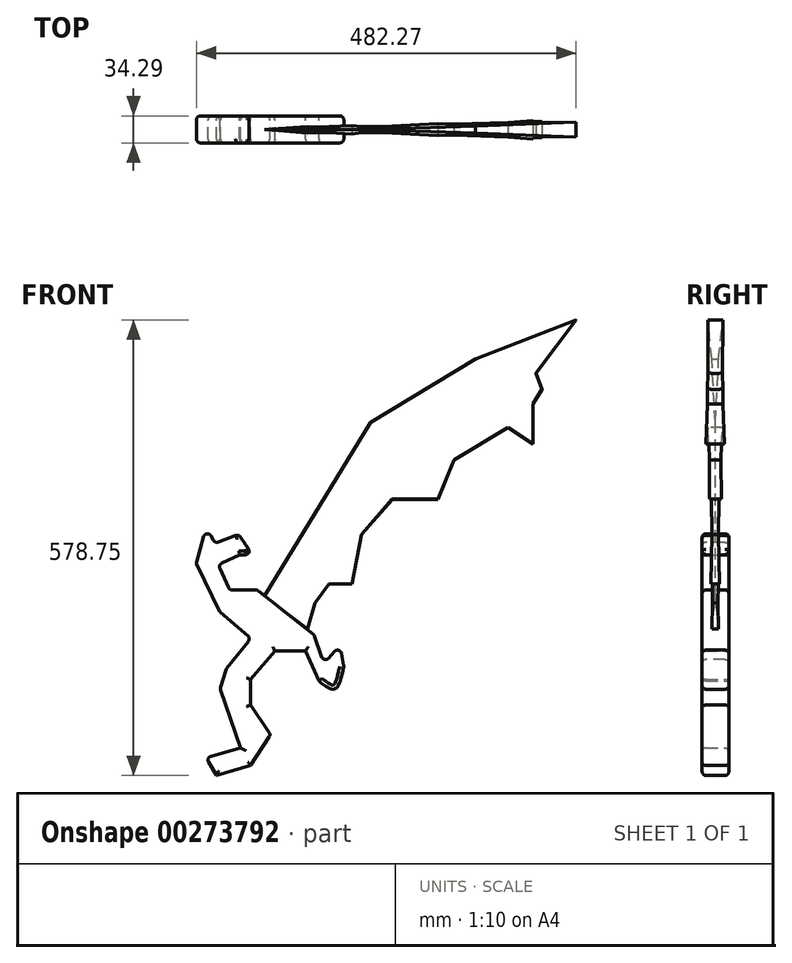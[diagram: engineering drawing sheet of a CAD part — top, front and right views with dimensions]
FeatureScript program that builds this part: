
annotation { "Feature Type Name" : "Feature", "Feature Type Description" : "" }
export const myFeature = defineFeature(function(context is Context, id is Id, definition is map)
    precondition{}
    {
        {
            var Q0;
            Q0=qCreatedBy(makeId("Front.planeOp"),FACE);
            var sketch = newSketch(context, id + "F0", { "sketchPlane" : qUnion([Q0])});
            skLineSegment(sketch, "E0", {"start": v(-57, -87.42) * mm, "end": v(-43.3, -110.26) * mm});
            skLineSegment(sketch, "E1", {"start": v(-43.3, -110.26) * mm, "end": v(0, -97.55) * mm});
            skLineSegment(sketch, "E2", {"start": v(0, -97.55) * mm, "end": v(25.23, -58.18) * mm});
            skLineSegment(sketch, "E3", {"start": v(25.23, -58.18) * mm, "end": v(0, -20.72) * mm});
            skLineSegment(sketch, "E4", {"start": v(0, -20.72) * mm, "end": v(0, 11.8) * mm});
            skLineSegment(sketch, "E5", {"start": v(0, 11.8) * mm, "end": v(30.53, 48) * mm});
            skLineSegment(sketch, "E6", {"start": v(30.53, 48) * mm, "end": v(69.5, 48) * mm});
            skLineSegment(sketch, "E7", {"start": v(69.5, 48) * mm, "end": v(86.38, 9.84) * mm});
            skFitSpline(sketch, "E8", {"points": [v(86.38, 9.84) * mm, v(107.27, 0) * mm, v(118.33, 28.28) * mm], "startDerivative": vector(47.46, -35.53) * mm, "endDerivative": vector(16.98, 59.13) * mm});
            skLineSegment(sketch, "E9", {"start": v(118.33, 28.28) * mm, "end": v(113.1, 55.2) * mm});
            skLineSegment(sketch, "E10", {"start": v(113.1, 55.2) * mm, "end": v(93.02, 32.3) * mm});
            skLineSegment(sketch, "E11", {"start": v(93.02, 32.3) * mm, "end": v(80.56, 68.05) * mm});
            skLineSegment(sketch, "E12", {"start": v(80.56, 68.05) * mm, "end": v(8.18, 125.56) * mm});
            skLineSegment(sketch, "E13", {"start": v(8.18, 125.56) * mm, "end": v(-26.99, 125.56) * mm});
            skLineSegment(sketch, "E14", {"start": v(-26.99, 125.56) * mm, "end": v(-41.25, 157.66) * mm});
            skLineSegment(sketch, "E15", {"start": v(-41.25, 157.66) * mm, "end": v(-14.06, 169.74) * mm});
            skFitSpline(sketch, "E16", {"points": [v(-14.06, 169.74) * mm, v(-14.06, 196.72) * mm], "startDerivative": vector(80.56, -0.17) * mm, "endDerivative": vector(0, 30.3) * mm});
            skLineSegment(sketch, "E17", {"start": v(-14.06, 196.72) * mm, "end": v(-45.08, 184.85) * mm});
            skLineSegment(sketch, "E18", {"start": v(-45.08, 184.85) * mm, "end": v(-56.75, 204.93) * mm});
            skLineSegment(sketch, "E19", {"start": v(-56.75, 204.93) * mm, "end": v(-69.38, 158.93) * mm});
            skLineSegment(sketch, "E20", {"start": v(-69.38, 158.93) * mm, "end": v(-38.92, 97.59) * mm});
            skLineSegment(sketch, "E21", {"start": v(-38.92, 97.59) * mm, "end": v(0, 64.25) * mm});
            skLineSegment(sketch, "E22", {"start": v(0, 64.25) * mm, "end": v(-31.42, 24.96) * mm});
            skLineSegment(sketch, "E23", {"start": v(-31.42, 24.96) * mm, "end": v(-38.73, 0) * mm});
            skLineSegment(sketch, "E24", {"start": v(-38.73, 0) * mm, "end": v(-12.81, -75.2) * mm});
            skLineSegment(sketch, "E25", {"start": v(-12.81, -75.2) * mm, "end": v(-57, -87.42) * mm});
            skPoint(sketch, "E26", {"position": v(-38.73, 0) * mm});
            skPoint(sketch, "E27", {"position": v(-19.17, -56.76) * mm});
            skSolve(sketch);
        }
        {
            var Q0;
            Q0=makeQuery(id+"F0.imprint","IMPRINT",FACE,{"disambiguationData":[TD([[makeQuery(id+"F0.imprint","IMPRINT",EDGE,{"derivedFrom":sQuery(id+"F0.wireOp",EDGE,"E0")}),1.0]])]});
            extrude(context, id + "F1", {"entities" : qUnion([Q0]), "depth" : 34.3 * mm});
        }
        {
            var Q0;
            Q0=makeQuery(id+"F1.opExtrude","SWEPT_EDGE",EDGE,{"disambiguationData":[OSD([sQuery(id+"F0.wireOp",EDGE,"E2"),sQuery(id+"F0.wireOp",EDGE,"E3")])]});
            var Q1;
            Q1=makeQuery(id+"F1.opExtrude","CAP_EDGE",EDGE,{"disambiguationData":[OSD([sQuery(id+"F0.wireOp",EDGE,"E5")])],"isStart":false});
            var Q2;
            Q2=makeQuery(id+"F1.opExtrude","CAP_EDGE",EDGE,{"disambiguationData":[OSD([sQuery(id+"F0.wireOp",EDGE,"E6")])],"isStart":false});
            var Q3;
            Q3=makeQuery(id+"F1.opExtrude","CAP_FACE",FACE,{"disambiguationData":[OSD([sQuery(id+"F0.wireOp",EDGE,"E0"),sQuery(id+"F0.wireOp",EDGE,"E1"),sQuery(id+"F0.wireOp",EDGE,"E2"),sQuery(id+"F0.wireOp",EDGE,"E3"),sQuery(id+"F0.wireOp",EDGE,"E4"),sQuery(id+"F0.wireOp",EDGE,"E5"),sQuery(id+"F0.wireOp",EDGE,"E6"),sQuery(id+"F0.wireOp",EDGE,"E7"),sQuery(id+"F0.wireOp",EDGE,"E8"),sQuery(id+"F0.wireOp",EDGE,"E9"),sQuery(id+"F0.wireOp",EDGE,"E10"),sQuery(id+"F0.wireOp",EDGE,"E11"),sQuery(id+"F0.wireOp",EDGE,"E12"),sQuery(id+"F0.wireOp",EDGE,"E13"),sQuery(id+"F0.wireOp",EDGE,"E14"),sQuery(id+"F0.wireOp",EDGE,"E15"),sQuery(id+"F0.wireOp",EDGE,"E16"),sQuery(id+"F0.wireOp",EDGE,"E17"),sQuery(id+"F0.wireOp",EDGE,"E18"),sQuery(id+"F0.wireOp",EDGE,"E19"),sQuery(id+"F0.wireOp",EDGE,"E20"),sQuery(id+"F0.wireOp",EDGE,"E21"),sQuery(id+"F0.wireOp",EDGE,"E22"),sQuery(id+"F0.wireOp",EDGE,"E23"),sQuery(id+"F0.wireOp",EDGE,"E24"),sQuery(id+"F0.wireOp",EDGE,"E25")])],"isStart":false});
            var Q4;
            Q4=makeQuery(id+"F1.opExtrude","SWEPT_FACE",FACE,{"disambiguationData":[OSD([sQuery(id+"F0.wireOp",EDGE,"E12")])]});
            var Q5;
            Q5=makeQuery(id+"F1.opExtrude","SWEPT_FACE",FACE,{"disambiguationData":[OSD([sQuery(id+"F0.wireOp",EDGE,"E13")])]});
            var Q6;
            Q6=makeQuery(id+"F1.opExtrude","SWEPT_FACE",FACE,{"disambiguationData":[OSD([sQuery(id+"F0.wireOp",EDGE,"E14")])]});
            var Q7;
            Q7=makeQuery(id+"F1.opExtrude","SWEPT_FACE",FACE,{"disambiguationData":[OSD([sQuery(id+"F0.wireOp",EDGE,"E18")])]});
            var Q8;
            Q8=makeQuery(id+"F1.opExtrude","SWEPT_EDGE",EDGE,{"disambiguationData":[OSD([sQuery(id+"F0.wireOp",EDGE,"E16"),sQuery(id+"F0.wireOp",EDGE,"E17")])]});
            var Q9;
            Q9=makeQuery(id+"F1.opExtrude","SWEPT_EDGE",EDGE,{"disambiguationData":[OSD([sQuery(id+"F0.wireOp",EDGE,"E8"),sQuery(id+"F0.wireOp",EDGE,"E9")])]});
            var Q10;
            Q10=makeQuery(id+"F1.opExtrude","SWEPT_EDGE",EDGE,{"disambiguationData":[OSD([sQuery(id+"F0.wireOp",EDGE,"E9"),sQuery(id+"F0.wireOp",EDGE,"E10")])]});
            var Q11;
            Q11=makeQuery(id+"F1.opExtrude","SWEPT_FACE",FACE,{"disambiguationData":[OSD([sQuery(id+"F0.wireOp",EDGE,"E11")])]});
            var Q12;
            Q12=makeQuery(id+"F1.opExtrude","CAP_FACE",FACE,{"disambiguationData":[OSD([sQuery(id+"F0.wireOp",EDGE,"E0"),sQuery(id+"F0.wireOp",EDGE,"E1"),sQuery(id+"F0.wireOp",EDGE,"E2"),sQuery(id+"F0.wireOp",EDGE,"E3"),sQuery(id+"F0.wireOp",EDGE,"E4"),sQuery(id+"F0.wireOp",EDGE,"E5"),sQuery(id+"F0.wireOp",EDGE,"E6"),sQuery(id+"F0.wireOp",EDGE,"E7"),sQuery(id+"F0.wireOp",EDGE,"E8"),sQuery(id+"F0.wireOp",EDGE,"E9"),sQuery(id+"F0.wireOp",EDGE,"E10"),sQuery(id+"F0.wireOp",EDGE,"E11"),sQuery(id+"F0.wireOp",EDGE,"E12"),sQuery(id+"F0.wireOp",EDGE,"E13"),sQuery(id+"F0.wireOp",EDGE,"E14"),sQuery(id+"F0.wireOp",EDGE,"E15"),sQuery(id+"F0.wireOp",EDGE,"E16"),sQuery(id+"F0.wireOp",EDGE,"E17"),sQuery(id+"F0.wireOp",EDGE,"E18"),sQuery(id+"F0.wireOp",EDGE,"E19"),sQuery(id+"F0.wireOp",EDGE,"E20"),sQuery(id+"F0.wireOp",EDGE,"E21"),sQuery(id+"F0.wireOp",EDGE,"E22"),sQuery(id+"F0.wireOp",EDGE,"E23"),sQuery(id+"F0.wireOp",EDGE,"E24"),sQuery(id+"F0.wireOp",EDGE,"E25")])],"isStart":true});
            var Q13;
            Q13=makeQuery(id+"F1.opExtrude","SWEPT_EDGE",EDGE,{"disambiguationData":[OSD([sQuery(id+"F0.wireOp",EDGE,"E0"),sQuery(id+"F0.wireOp",EDGE,"E25")])]});
            var Q14;
            Q14=makeQuery(id+"F1.opExtrude","SWEPT_EDGE",EDGE,{"disambiguationData":[OSD([sQuery(id+"F0.wireOp",EDGE,"E23"),sQuery(id+"F0.wireOp",EDGE,"E24")])]});
            var Q15;
            Q15=makeQuery(id+"F1.opExtrude","SWEPT_EDGE",EDGE,{"disambiguationData":[OSD([sQuery(id+"F0.wireOp",EDGE,"E22"),sQuery(id+"F0.wireOp",EDGE,"E23")])]});
            var Q16;
            Q16=makeQuery(id+"F1.opExtrude","SWEPT_EDGE",EDGE,{"disambiguationData":[OSD([sQuery(id+"F0.wireOp",EDGE,"E21"),sQuery(id+"F0.wireOp",EDGE,"E22")])]});
            var Q17;
            Q17=makeQuery(id+"F1.opExtrude","SWEPT_EDGE",EDGE,{"disambiguationData":[OSD([sQuery(id+"F0.wireOp",EDGE,"E20"),sQuery(id+"F0.wireOp",EDGE,"E21")])]});
            var Q18;
            Q18=makeQuery(id+"F1.opExtrude","SWEPT_EDGE",EDGE,{"disambiguationData":[OSD([sQuery(id+"F0.wireOp",EDGE,"E19"),sQuery(id+"F0.wireOp",EDGE,"E20")])]});
            fillet(context, id + "F2", {"entities" : qUnion([Q0, Q1, Q2, Q3, Q4, Q5, Q6, Q7, Q8, Q9, Q10, Q11, Q12, Q13, Q14, Q15, Q16, Q17, Q18]), "radius" : 5.08 * mm, "tangentPropagation" : true, "allowEdgeOverflow" : false});
        }
        {
            var Q0;
            Q0=qCreatedBy(makeId("Front.planeOp"),FACE);
            cPlane(context, id + "F3", {"entities" : qUnion([Q0]), "cplaneType" : CPlaneType.OFFSET, "offset" : 17.53 * mm, "width" : 152.4 * mm, "height" : 152.4 * mm});
        }
        {
            var Q0;
            Q0=qCreatedBy(id+"F3.planeOp",FACE);
            var sketch = newSketch(context, id + "F4", { "sketchPlane" : qUnion([Q0])});
            skLineSegment(sketch, "E28", {"start": v(17.46, 117.6) * mm, "end": v(152.28, 338.54) * mm});
            skLineSegment(sketch, "E29", {"start": v(152.28, 338.54) * mm, "end": v(285.25, 418.57) * mm});
            skLineSegment(sketch, "E30", {"start": v(285.25, 418.57) * mm, "end": v(413.22, 468.34) * mm});
            skLineSegment(sketch, "E31", {"start": v(71.96, 76.13) * mm, "end": v(81.44, 109.31) * mm});
            skLineSegment(sketch, "E32", {"start": v(81.44, 109.31) * mm, "end": v(99.56, 133) * mm});
            skLineSegment(sketch, "E33", {"start": v(99.56, 133) * mm, "end": v(128.84, 133) * mm});
            skLineSegment(sketch, "E34", {"start": v(128.84, 133) * mm, "end": v(140.69, 195.81) * mm});
            skLineSegment(sketch, "E35", {"start": v(140.69, 195.81) * mm, "end": v(179.79, 240.84) * mm});
            skLineSegment(sketch, "E36", {"start": v(179.79, 240.84) * mm, "end": v(237.85, 240.84) * mm});
            skLineSegment(sketch, "E37", {"start": v(237.85, 240.84) * mm, "end": v(258.08, 290.4) * mm});
            skLineSegment(sketch, "E38", {"start": v(258.08, 290.4) * mm, "end": v(326.72, 331.72) * mm});
            skLineSegment(sketch, "E39", {"start": v(326.72, 331.72) * mm, "end": v(358.71, 311.06) * mm});
            skPoint(sketch, "E39.endSnap0", {"position": v(292.4, 311.06) * mm});
            skLineSegment(sketch, "E40", {"start": v(358.71, 311.06) * mm, "end": v(358.71, 361.7) * mm});
            skLineSegment(sketch, "E41", {"start": v(358.71, 361.7) * mm, "end": v(370.17, 380.47) * mm});
            skLineSegment(sketch, "E42", {"start": v(370.17, 380.47) * mm, "end": v(362.27, 400.8) * mm});
            skLineSegment(sketch, "E43", {"start": v(362.27, 400.8) * mm, "end": v(413.22, 468.34) * mm});
            skLineSegment(sketch, "E44", {"start": v(71.96, 76.13) * mm, "end": v(17.46, 117.6) * mm});
            skSolve(sketch);
        }
        {
            var Q0;
            Q0=makeQuery(id+"F4.imprint","IMPRINT",FACE,{"disambiguationData":[TD([[makeQuery(id+"F4.imprint","IMPRINT",EDGE,{"derivedFrom":sQuery(id+"F4.wireOp",EDGE,"E28")}),-1.0]])]});
            var Q1;
            Q1=sQuery(id+"F4.wireOp",EDGE,"E28");
            revolve(context, id + "F5", {"operationType" : NewBodyOperationType.ADD, "entities" : qUnion([Q0]), "axis" : qUnion([Q1]), "revolveType" : RevolveType.TWO_DIRECTIONS, "angle" : 3.5 * degree, "angleBack" : 356.5 * degree});
        }
    });
